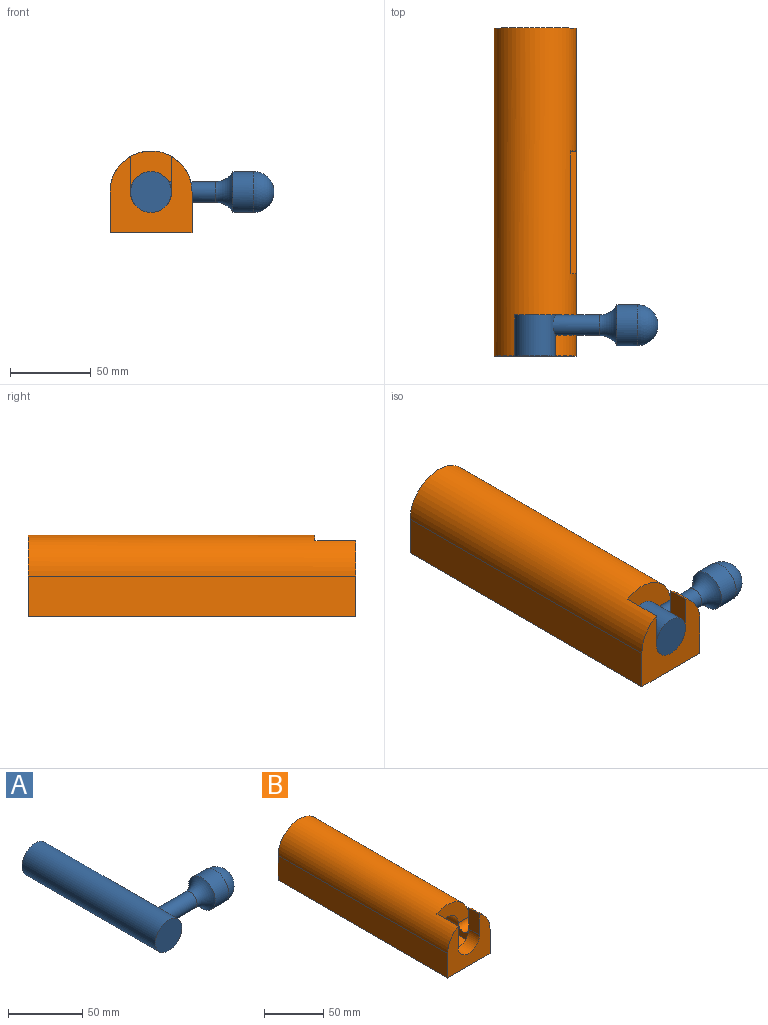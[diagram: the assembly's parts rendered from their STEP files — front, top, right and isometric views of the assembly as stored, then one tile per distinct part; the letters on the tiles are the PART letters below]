
ASSEMBLY  parts=2 mates=1
PART A: 7 faces, bbox 88.9x128.6x41.2 mm
  f0: cylinder r=12.7mm len=127mm, axis (0,1,0), area 10003.1mm2, adj f1,f2,f3
  f1: plane 25.4x25.4mm, normal (0,1,0), area 506.7mm2, adj f0
  f2: plane 25.4x25.4mm, normal (0,-1,0), area 506.7mm2, adj f0
  f3: cylinder r=6.35mm len=28.8mm, axis (-1,0,0), area 1114.6mm2, adj f0,f6
  f4: cylinder r=12.7mm len=25.4mm, axis (-1,0,0), area 1013.4mm2, adj f5,f6
  f5: sphere r=12.7mm, area 1013.4mm2, adj f4
  f6: torus R=19.05mm, axis (1,0,0), area 714.2mm2, adj f3,f4
PART B: 29 faces, bbox 50.8x203.2x50.8 mm
  f0: plane 203.2x25.4mm, normal (1,0,0), area 4130.2mm2, adj f4,f5,f7,f8,f18,f19,f21,f22
  f1: plane 12.7x12.7mm, normal (0,-1,0), area 34.6mm2, adj f3,f6,f27
  f2: plane 12.7x12.7mm, normal (0,1,0), area 34.6mm2, adj f3,f13,f27
  f3: plane 25.4x12.7mm, normal (0,0,1), area 322.6mm2, adj f1,f2,f10,f16,f17,f27
  f4: plane 203.2x50.8mm, normal (0,0,-1), area 8387.1mm2, adj f0,f8,f14,f19,f20,f21,f22,f26
  f5: plane 76.2x12.7mm, normal (0,0,1), area 967.7mm2, adj f0,f21,f22,f26
  f6: cylinder r=12.7mm len=25.4mm, axis (0,1,0), area 2026.8mm2, adj f1,f9,f17,f21,f24
  f7: cylinder r=25.4mm len=203.2mm, axis (0,-1,0), area 13850mm2, adj f0,f8,f9,f10,f14,f19,f21,f22
  f8: plane 50.8x47.4mm, normal (0,-1,0), area 1433.2mm2, adj f0,f4,f7,f10,f12,f13,f14,f18
  f9: plane 38.1x25.4mm, normal (0,-1,0), area 561.9mm2, adj f6,f7,f10,f28
  f10: plane 34.7x25.4mm, normal (1,0,0), area 720mm2, adj f3,f7,f8,f9,f13,f16,f17
  f11: plane 22x12.7mm, normal (0,1,0), area 198.1mm2, adj f12,f18,f28
  f12: plane 22x12.7mm, normal (-1,0,0), area 279.4mm2, adj f8,f11,f13,f18
  f13: cylinder r=12.7mm len=25.4mm, axis (0,1,0), area 506.7mm2, adj f2,f8,f10,f12,f16
  f14: plane 203.2x25.4mm, normal (-1,0,0), area 5161.3mm2, adj f4,f7,f8,f19
  f15: cylinder r=12.7mm len=76.2mm, axis (0,1,0), area 6080.5mm2, adj f19,f22,f25
  f16: plane 12.7x12.7mm, normal (0,1,0), area 34.6mm2, adj f3,f10,f13
  f17: plane 12.7x12.7mm, normal (0,-1,0), area 34.6mm2, adj f3,f6,f10
  f18: cylinder r=25.4mm len=22mm, axis (0,-1,0), area 337.8mm2, adj f0,f8,f11,f12
  f19: plane 50.8x50.8mm, normal (0,1,0), area 1797mm2, adj f0,f4,f7,f14,f15
  f20: plane 76.2x38.1mm, normal (1,0,0), area 2903.2mm2, adj f4,f21,f22,f23,f24,f25
  f21: plane 38.1x38.1mm, normal (0,1,0), area 735mm2, adj f0,f4,f5,f6,f7,f20,f23,f26
  f22: plane 38.1x38.1mm, normal (0,-1,0), area 735mm2, adj f0,f4,f5,f7,f15,f20,f23,f26
  f23: plane 76.2x34.7mm, normal (0,0,-1), area 2643.9mm2, adj f7,f20,f21,f22,f24,f25
  f24: plane 12.7x12.7mm, normal (0,1,0), area 34.6mm2, adj f6,f20,f23
  f25: plane 12.7x12.7mm, normal (0,-1,0), area 34.6mm2, adj f15,f20,f23
  f26: plane 76.2x12.7mm, normal (-1,0,0), area 967.7mm2, adj f4,f5,f21,f22
  f27: plane 12.7x12.7mm, normal (-1,0,0), area 98mm2, adj f1,f2,f3,f28
  f28: cylinder r=6.35mm len=12.7mm, axis (1,0,0), area 253.4mm2, adj f0,f9,f11,f27
PLACE A rot(axis=(0,-1,0),0deg) t=(-100.5,15.89,8.72)mm
PLACE B t=(-125.9,15.89,-16.68)mm fixed
MATE cylindrical A.f0 <-> B.f6  axis (0,-1,0) through (-100.5,-111.11,8.72)mm
